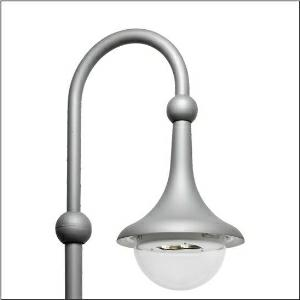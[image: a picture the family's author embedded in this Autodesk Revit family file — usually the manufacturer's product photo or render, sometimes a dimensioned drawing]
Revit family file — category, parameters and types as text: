
# Revit family: grosse_glocke_iq___st1_2a_5xa1565k1f108_5d30
name_source: partatom
category: Lighting Fixtures
units: mm (PartAtom-declared; Revit-internal decimal feet)

## family parameters
Cut with Voids When Loaded = No
Host = Face
Light Source = No
Part Type = Normal
Room Calculation Point = No
Round Connector Dimension = Use Diameter
Shared = No

## types (1)
- --- (1 x LED, 5420 lm, 34.3 W, 4000K)
    Apparent Load = 34 VA
    CIE Flux Codes = 28 66 95 100 100
    Color Rendering = 70
    Color Temperature = 4000K
    Default Elevation = 1800 mm
    Description = Large Bell iQ, mast luminaire, primary light control with 3 zone facetted reflector, of plastic, silver coated, primary optical cover: enclosure, of PMMA, transparent, light distribution: ST1.2a, light emission: direct distribution, primary light characteristic: asymmetric, installation type: suspended mounting, High Power LED, rated luminous flux: 5.420lm, luminous efficacy: 158lm/W, light colour: 740, colour temperature: 4000K, control gear: iQ Street-Remote, control: optimised constant luminous flux control (CLO 2.0), Desk-Remote (wireless, voltage-free reading and setting of iQ features in the workshop via application-optimized NFC function/RFID function), Light-Fading, Smart-Wire, Night-Set, Lumen-Switch, Temp-Guard, Auto-Match, Street-Remote, pre-setting: logarithmic dimming characteristic, mains connection: 230..240V, AC, 50/60Hz, start of lifetime: 34W, end of service life: 38W, reduction: 16W, luminaire housing, bell-shaped, of glass-fibre reinforced polyester, coated, Siteco® metallic grey (DB 702S), please order curved mast extension separately, diameter: 530mm, height: 695mm, mounting height: 4..6m, protection rating (complete): IP54, insulation class (complete): insulation class II (safety insulation), certification: CE, ENEC, VDE, impact resistance: IK08, standard-compliant lighting for roads and squares, packaging unit: 1 piece

Light Distribution: ST1.2a
    Height = 695 mm
    Lamp = 1 x LED
    Lamp Light Flux = 5420 lm
    Lamp Power = 34.3 W
    Lamp count = 1
    Length = 530 mm
    Luminous efficacy = 158 lm/W
    Manufacturer = Siteco
    ModVariant = No
    Model = 5XA1565K1F108
    Number of Poles = 1
    OnlyDefault = Yes
    Power Factor = 1
    Product Name = Große Glocke iQ | ST1.2a
    Product group = mast luminaire | pylon annexe
    ProductGroupID = 6200
    Protection Class = Protection class II
    Protection Degree = IP 54
    RLX_Detail_Level = 1
    RLX_Emergency_Light_Flux = 0 lm
    RLX_Emergency_Type = 0
    RLX_Emergency_Type_DB = No
    RlxData = <blob elided: 85393 chars, md5=65ea398b>
    Socket = socket
    Standby Power = 0 W
    System Light Flux = 5420 lm
    System Power = 34 W
    Type Comments = factory setting: luminous flux: 100 % | dim-lin: 254 | 640 mA
    Type Image = l_1347688.jpg
    URL = http://relux.com
    VarID = @adj_066199
    Voltage = 0 V
    Weight = 0.00 kg
    Width = 0 mm  [stored 0 ft]

note: [stored X ft] marks values corroborated as IEEE doubles in the binary element streams (Revit-internal decimal feet)

## geometry (parser evidence)
native form markers: Blend x4, Sweep x12
no freeform markers — native parametric forms only
